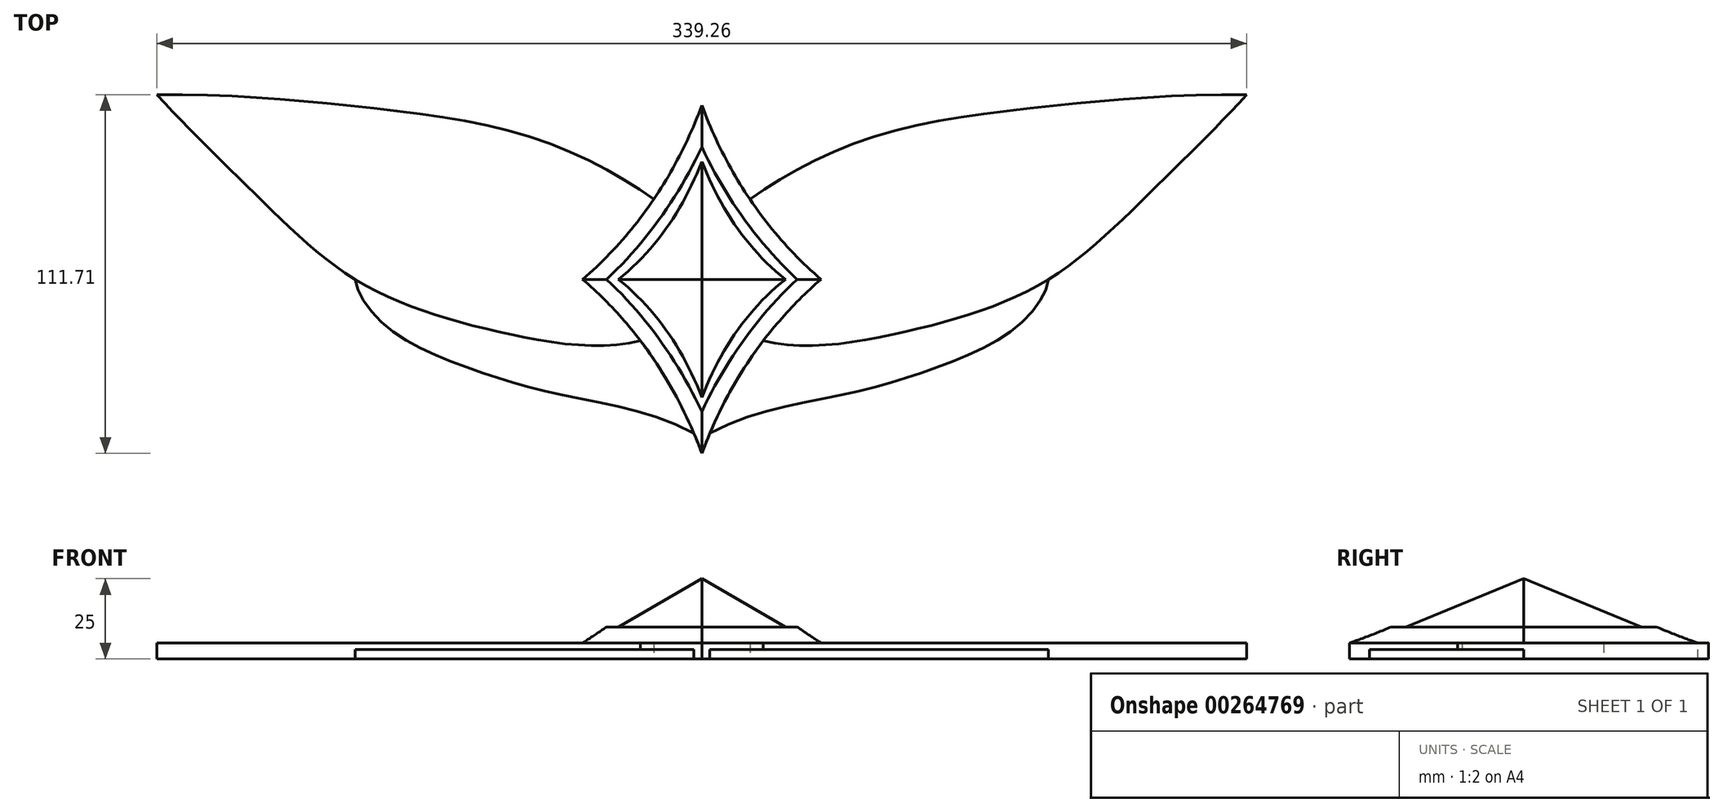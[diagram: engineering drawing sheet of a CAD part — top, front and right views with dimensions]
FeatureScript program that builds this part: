
annotation { "Feature Type Name" : "Feature", "Feature Type Description" : "" }
export const myFeature = defineFeature(function(context is Context, id is Id, definition is map)
    precondition{}
    {
        {
            var Q0;
            Q0=qCreatedBy(makeId("Top.planeOp"),FACE);
            var sketch = newSketch(context, id + "F0", { "sketchPlane" : qUnion([Q0])});
            skLineSegment(sketch, "E0", {"start": v(0, 55.19) * mm, "end": v(0, -54.81) * mm, "construction": true});
            skSolve(sketch);
        }
        {
            var Q0;
            Q0=qCreatedBy(makeId("Top.planeOp"),FACE);
            var sketch = newSketch(context, id + "F1", { "sketchPlane" : qUnion([Q0])});
            skFitSpline(sketch, "E1", {"points": [v(0, 36.7) * mm, v(-26.02, 0) * mm], "startDerivative": vector(-16.98, -43.47) * mm, "endDerivative": vector(-35.6, -28.2) * mm});
            skFitSpline(sketch, "E2.MirrorCS", {"points": [v(0, -36.7) * mm, v(-26.02, 0) * mm], "startDerivative": vector(-16.98, 43.47) * mm, "endDerivative": vector(-35.6, 28.2) * mm});
            skFitSpline(sketch, "E3.MirrorCS", {"points": [v(0, 36.7) * mm, v(26.02, 0) * mm], "startDerivative": vector(16.98, -43.47) * mm, "endDerivative": vector(35.6, -28.2) * mm});
            skFitSpline(sketch, "E4.MirrorCS", {"points": [v(0, -36.7) * mm, v(26.02, 0) * mm], "startDerivative": vector(16.98, 43.47) * mm, "endDerivative": vector(35.6, 28.2) * mm});
            skSolve(sketch);
        }
        {
            var Q0;
            Q0=qCreatedBy(makeId("Top.planeOp"),FACE);
            cPlane(context, id + "F2", {"entities" : qUnion([Q0]), "cplaneType" : CPlaneType.OFFSET, "offset" : 15 * mm, "width" : 150 * mm, "height" : 150 * mm});
        }
        {
            var Q0;
            Q0=qCreatedBy(id+"F2.planeOp",FACE);
            var sketch = newSketch(context, id + "F3", { "sketchPlane" : qUnion([Q0])});
            skPoint(sketch, "E5", {"position": v(0, 0) * mm});
            skSolve(sketch);
        }
        {
            var Q0;
            Q0=makeQuery(id+"F1.imprint","IMPRINT",FACE,{"disambiguationData":[TD([[makeQuery(id+"F1.imprint","IMPRINT",EDGE,{"derivedFrom":sQuery(id+"F1.wireOp",EDGE,"E1")}),1.0]])]});
            var Q1;
            Q1=sQuery(id+"F3.wireOp",VERTEX,"E5");
            loft(context, id + "F4", {"sheetProfilesArray" : [{ "sheetProfileEntities" : qUnion([Q0]) }, { "sheetProfileEntities" : qUnion([Q1]) }]});
        }
        {
            var Q0;
            Q0=qCreatedBy(makeId("Top.planeOp"),FACE);
            var sketch = newSketch(context, id + "F5", { "sketchPlane" : qUnion([Q0])});
            skFitSpline(sketch, "E6", {"points": [v(0, 54.2) * mm, v(-37.1, 0) * mm], "startDerivative": vector(-23.47, -63.43) * mm, "endDerivative": vector(-50.48, -43.42) * mm});
            skFitSpline(sketch, "E7.MirrorCS", {"points": [v(0, -54.2) * mm, v(-37.1, 0) * mm], "startDerivative": vector(-23.47, 63.43) * mm, "endDerivative": vector(-50.48, 43.42) * mm});
            skFitSpline(sketch, "E8.MirrorCS", {"points": [v(0, 54.2) * mm, v(37.1, 0) * mm], "startDerivative": vector(23.47, -63.43) * mm, "endDerivative": vector(50.48, -43.42) * mm});
            skFitSpline(sketch, "E9.MirrorCS", {"points": [v(0, -54.2) * mm, v(37.1, 0) * mm], "startDerivative": vector(23.47, 63.43) * mm, "endDerivative": vector(50.48, 43.42) * mm});
            skSolve(sketch);
        }
        {
            var Q0;
            Q0 = qSketchRegion(id + "F5", true);
            extrude(context, id + "F6", {"entities" : qUnion([Q0]), "operationType" : NewBodyOperationType.ADD, "oppositeDirection" : true, "depth" : 8 * mm, "offsetDistance" : 25 * mm});
        }
        {
            var Q0;
            Q0=makeQuery(id+"F6.opExtrude","CAP_EDGE",EDGE,{"disambiguationData":[OSD([sQuery(id+"F5.wireOp",EDGE,"E6")])],"isStart":true});
            var Q1;
            Q1=makeQuery(id+"F6.opExtrude","CAP_EDGE",EDGE,{"disambiguationData":[OSD([sQuery(id+"F5.wireOp",EDGE,"E7.MirrorCS")])],"isStart":true});
            var Q2;
            Q2=makeQuery(id+"F6.opExtrude","CAP_EDGE",EDGE,{"disambiguationData":[OSD([sQuery(id+"F5.wireOp",EDGE,"E8.MirrorCS")])],"isStart":true});
            var Q3;
            Q3=makeQuery(id+"F6.opExtrude","CAP_EDGE",EDGE,{"disambiguationData":[OSD([sQuery(id+"F5.wireOp",EDGE,"E9.MirrorCS")])],"isStart":true});
            chamfer(context, id + "F7", {"entities" : qUnion([Q0, Q1, Q2, Q3]), "width" : 5 * mm, "tangentPropagation" : true});
        }
        {
            var Q0;
            Q0=makeQuery(id+"F6.opExtrude","CAP_FACE",FACE,{"disambiguationData":[OSD([sQuery(id+"F5.wireOp",EDGE,"E6"),sQuery(id+"F5.wireOp",EDGE,"E7.MirrorCS"),sQuery(id+"F5.wireOp",EDGE,"E8.MirrorCS"),sQuery(id+"F5.wireOp",EDGE,"E9.MirrorCS")])],"isStart":false});
            var sketch = newSketch(context, id + "F8", { "sketchPlane" : qUnion([Q0])});
            skFitSpline(sketch, "E10", {"points": [v(14.97, -24.91) * mm, v(52.46, -44.03) * mm, v(106.85, -53.77) * mm, v(169.63, -57.46) * mm], "startDerivative": vector(98.2, -71.22) * mm, "endDerivative": vector(185.06, 2.83) * mm});
            skFitSpline(sketch, "E11", {"points": [v(169.63, -57.46) * mm, v(140.76, -28.25) * mm, v(107.92, 0) * mm, v(65.9, 15.72) * mm, v(19.08, 19.17) * mm], "startDerivative": vector(-116.53, 126.45) * mm, "endDerivative": vector(-162.05, -39.66) * mm});
            skFitSpline(sketch, "E12", {"points": [v(107.92, 0) * mm, v(98.03, 14.8) * mm, v(72.04, 27.8) * mm, v(42.86, 36.13) * mm, v(2.46, 48) * mm], "startDerivative": vector(-9.86, 69.86) * mm, "endDerivative": vector(-130.95, 72.38) * mm});
            skFitSpline(sketch, "E13.MirrorCS", {"points": [v(-14.97, -24.91) * mm, v(-52.46, -44.03) * mm, v(-106.85, -53.77) * mm, v(-169.63, -57.46) * mm], "startDerivative": vector(-98.2, -71.22) * mm, "endDerivative": vector(-185.06, 2.83) * mm});
            skFitSpline(sketch, "E14.MirrorCS", {"points": [v(-169.63, -57.46) * mm, v(-140.76, -28.25) * mm, v(-107.92, 0) * mm, v(-65.9, 15.72) * mm, v(-19.08, 19.17) * mm], "startDerivative": vector(116.53, 126.45) * mm, "endDerivative": vector(162.05, -39.66) * mm});
            skFitSpline(sketch, "E15.MirrorCS", {"points": [v(-107.92, 0) * mm, v(-98.03, 14.8) * mm, v(-72.04, 27.8) * mm, v(-42.86, 36.13) * mm, v(-2.46, 48) * mm], "startDerivative": vector(9.86, 69.86) * mm, "endDerivative": vector(130.95, 72.38) * mm});
            skSolve(sketch);
        }
        {
            var Q0;
            {var subQ3=sQuery(id+"F8.wireOp",EDGE,"E10");Q0=makeQuery(id+"F8.imprint","IMPRINT",FACE,{"disambiguationData":[TD([[makeQuery(id+"F8.imprint","IMPRINT",EDGE,{"derivedFrom":subQ3}),1.0]])]});}
            var Q1;
            {var subQ4=sQuery(id+"F8.wireOp",EDGE,"E13.MirrorCS");Q1=makeQuery(id+"F8.imprint","IMPRINT",FACE,{"disambiguationData":[TD([[makeQuery(id+"F8.imprint","IMPRINT",EDGE,{"derivedFrom":subQ4}),-1.0]])]});}
            extrude(context, id + "F9", {"entities" : qUnion([Q0, Q1]), "operationType" : NewBodyOperationType.ADD, "oppositeDirection" : true, "depth" : 3 * mm, "offsetDistance" : 25 * mm});
        }
        {
            var Q0;
            {var subQ3=sQuery(id+"F8.wireOp",EDGE,"E15.MirrorCS");Q0=makeQuery(id+"F8.imprint","IMPRINT",FACE,{"disambiguationData":[TD([[makeQuery(id+"F8.imprint","IMPRINT",EDGE,{"derivedFrom":subQ3}),-1.0]])]});}
            var Q1;
            {var subQ3=sQuery(id+"F8.wireOp",EDGE,"E12");Q1=makeQuery(id+"F8.imprint","IMPRINT",FACE,{"disambiguationData":[TD([[makeQuery(id+"F8.imprint","IMPRINT",EDGE,{"derivedFrom":subQ3}),1.0]])]});}
            extrude(context, id + "F10", {"entities" : qUnion([Q0, Q1]), "operationType" : NewBodyOperationType.ADD, "oppositeDirection" : true, "depth" : 1 * mm, "offsetDistance" : 25 * mm});
        }
        {
            var Q0;
            {var subQ0=sQuery(id+"F8.wireOp",EDGE,"E14.MirrorCS");var subQ1=sQuery(id+"F5.wireOp",EDGE,"E7.MirrorCS");var subQ2=sQuery(id+"F8.wireOp",EDGE,"E11");var subQ3=sQuery(id+"F5.wireOp",EDGE,"E9.MirrorCS");var subQ4=sQuery(id+"F5.wireOp",EDGE,"E6");var subQ5=sQuery(id+"F5.wireOp",EDGE,"E8.MirrorCS");Q0=makeQuery(id+"F10.boolean.opBoolean","MERGE",FACE,{"derivedFrom":[makeQuery(id+"F9.boolean.opBoolean","MERGE",FACE,{"derivedFrom":[makeQuery(id+"F6.opExtrude","CAP_FACE",FACE,{"disambiguationData":[OSD([subQ4,subQ1,subQ5,subQ3])],"isStart":false}),makeQuery(id+"F9.opExtrude","CAP_FACE",FACE,{"disambiguationData":[OSD([subQ5,subQ3,sQuery(id+"F8.wireOp",EDGE,"E10"),subQ2])],"isStart":true}),makeQuery(id+"F9.opExtrude","CAP_FACE",FACE,{"disambiguationData":[OSD([subQ4,subQ1,sQuery(id+"F8.wireOp",EDGE,"E13.MirrorCS"),subQ0])],"isStart":true})]}),makeQuery(id+"F10.opExtrude","CAP_FACE",FACE,{"disambiguationData":[OSD([subQ3,subQ2,sQuery(id+"F8.wireOp",EDGE,"E12")])],"isStart":true}),makeQuery(id+"F10.opExtrude","CAP_FACE",FACE,{"disambiguationData":[OSD([subQ1,subQ0,sQuery(id+"F8.wireOp",EDGE,"E15.MirrorCS")])],"isStart":true})]});}
            extrude(context, id + "F11", {"entities" : qUnion([Q0]), "operationType" : NewBodyOperationType.ADD, "depth" : 2 * mm, "offsetDistance" : 25 * mm});
        }
    });
